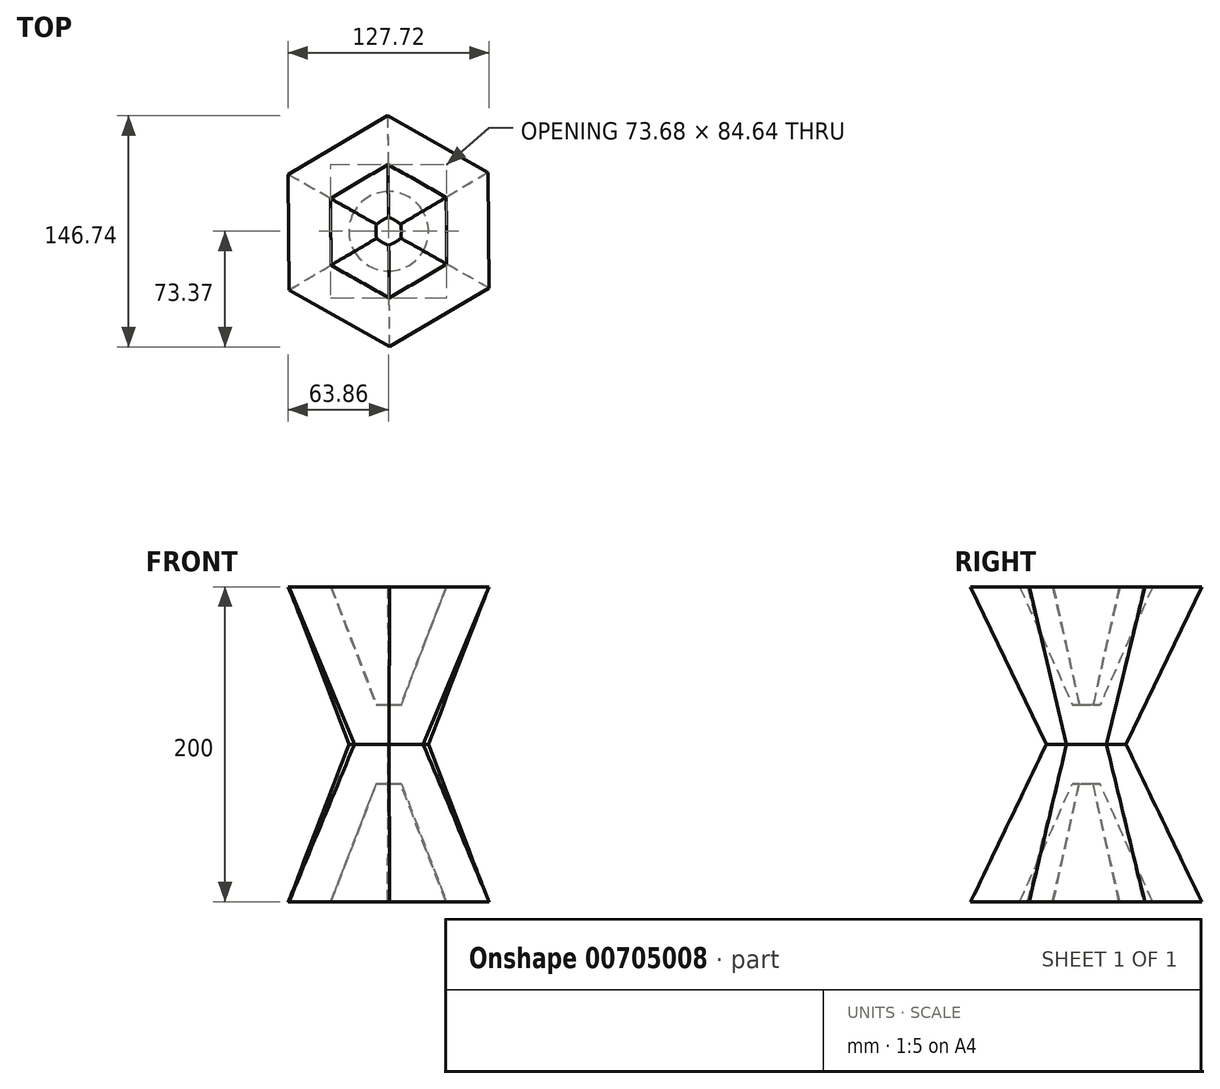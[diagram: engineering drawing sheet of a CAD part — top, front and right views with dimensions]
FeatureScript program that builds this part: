
annotation { "Feature Type Name" : "Feature", "Feature Type Description" : "" }
export const myFeature = defineFeature(function(context is Context, id is Id, definition is map)
    precondition{}
    {
        {
            var Q0;
            Q0=qCreatedBy(makeId("Top.planeOp"),FACE);
            cPlane(context, id + "F0", {"entities" : qUnion([Q0]), "cplaneType" : CPlaneType.OFFSET, "offset" : 100 * mm, "width" : 150 * mm, "height" : 150 * mm});
        }
        {
            var Q0;
            Q0=qCreatedBy(id+"F0.planeOp",FACE);
            var sketch = newSketch(context, id + "F1", { "sketchPlane" : qUnion([Q0])});
            skCircle(sketch, "E0.cCircle", {"center": v(0, 0) * mm, "radius": 63.54 * mm, "construction": true});
            skLineSegment(sketch, "E0.0", {"start": v(-63.86, 36.13) * mm, "end": v(-0.64, 73.37) * mm});
            skLineSegment(sketch, "E0.1", {"start": v(-0.64, 73.37) * mm, "end": v(63.22, 37.24) * mm});
            skLineSegment(sketch, "E0.2", {"start": v(63.22, 37.24) * mm, "end": v(63.86, -36.13) * mm});
            skLineSegment(sketch, "E0.3", {"start": v(63.86, -36.13) * mm, "end": v(0.64, -73.37) * mm});
            skLineSegment(sketch, "E0.4", {"start": v(0.64, -73.37) * mm, "end": v(-63.22, -37.24) * mm});
            skLineSegment(sketch, "E0.5", {"start": v(-63.22, -37.24) * mm, "end": v(-63.86, 36.13) * mm});
            skPoint(sketch, "E0.0.midPoint", {"position": v(-32.25, 54.75) * mm});
            skSolve(sketch);
        }
        {
            var Q0;
            Q0=qCreatedBy(makeId("Top.planeOp"),FACE);
            var sketch = newSketch(context, id + "F2", { "sketchPlane" : qUnion([Q0])});
            skCircle(sketch, "E1", {"center": v(0, 0) * mm, "radius": 25.27 * mm});
            skSolve(sketch);
        }
        {
            var Q0;
            Q0=makeQuery(id+"F1.imprint","IMPRINT",FACE,{"disambiguationData":[TD([[makeQuery(id+"F1.imprint","IMPRINT",EDGE,{"derivedFrom":sQuery(id+"F1.wireOp",EDGE,"E0.0")}),-1.0]])]});
            var Q1;
            Q1=makeQuery(id+"F2.imprint","IMPRINT",FACE,{"disambiguationData":[TD([[makeQuery(id+"F2.imprint","IMPRINT",EDGE,{"derivedFrom":sQuery(id+"F2.wireOp",EDGE,"E1")}),1.0]])]});
            loft(context, id + "F3", {"sheetProfilesArray" : [{ "sheetProfileEntities" : qUnion([Q0]) }, { "sheetProfileEntities" : qUnion([Q1]) }]});
        }
        {
            var Q0;
            Q0=makeQuery(id+"F3.opLoft","CAP_FACE",FACE,{"disambiguationData":[OSD([makeQuery(id+"F1.imprint","IMPRINT",FACE,{"disambiguationData":[TD([[makeQuery(id+"F1.imprint","IMPRINT",EDGE,{"derivedFrom":sQuery(id+"F1.wireOp",EDGE,"E0.0")}),-1.0]])]})])],"isStart":true});
            shell(context, id + "F4", {"entities" : qUnion([Q0]), "thickness" : 25 * mm});
        }
        {
            var Q0;
            Q0=makeQuery(id+"F3.opLoft","SWEPT_BODY",BODY,{"disambiguationData":[OSD([makeQuery(id+"F1.imprint","IMPRINT",FACE,{"disambiguationData":[TD([[makeQuery(id+"F1.imprint","IMPRINT",EDGE,{"derivedFrom":sQuery(id+"F1.wireOp",EDGE,"E0.0")}),-1.0]])]}),makeQuery(id+"F2.imprint","IMPRINT",FACE,{"disambiguationData":[TD([[makeQuery(id+"F2.imprint","IMPRINT",EDGE,{"derivedFrom":sQuery(id+"F2.wireOp",EDGE,"E1")}),1.0]])]})])]});
            var Q1;
            Q1=qCreatedBy(makeId("Top.planeOp"),FACE);
            mirror(context, id + "F5", {"operationType" : NewBodyOperationType.ADD, "entities" : qUnion([Q0]), "mirrorPlane" : qUnion([Q1])});
        }
    });
